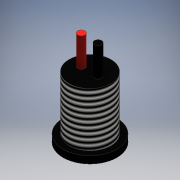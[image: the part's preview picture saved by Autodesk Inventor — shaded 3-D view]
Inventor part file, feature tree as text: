
AUTODESK INVENTOR PART (.ipt)
format: ipt  version: 2016 (Build 200138000, 138)  size: 154,112 bytes
history: native  units: mm
features: extrude x4, sketch x4, thread x1
ambient origin geometry x8: Origin, YZ Plane, XZ Plane, XY Plane, X Axis, Y Axis, Z Axis, Center Point
bodies: Solid1 (feature_tree)
feature tree (9):
  extrude  "Extrusion1"  Depth=37.0mm TaperAngle=0.0deg
  extrude  "Extrusion2"  Depth=5.0mm
  extrude  "Extrusion3"  Depth=37.0mm
  extrude  "Extrusion4"  Depth=4.0mm
  thread  "Thread1"  [1 undecoded]
  sketch  "Sketch1"  dims[d0=28.78mm d1=37.0mm d2=0.0mm]
  sketch  "Sketch2"  dims[d3=5.0mm d4=5.0mm]
  sketch  "Sketch3"  dims[d5=20.0mm d6=0.0mm d7=37.0mm]
  sketch  "Sketch4"  dims[d8=5.0mm d9=0.0mm d10=4.0mm d11=14.0mm d12=14.0mm d13=4.0mm d14=2.0mm d15=0.0mm d16=10.0mm d17=0.0mm]
note: 1 required parameter value undecoded (feature->parameter linkage not recoverable at this tier; creation-order binding heuristic only, values carry confidence <= 0.55)
